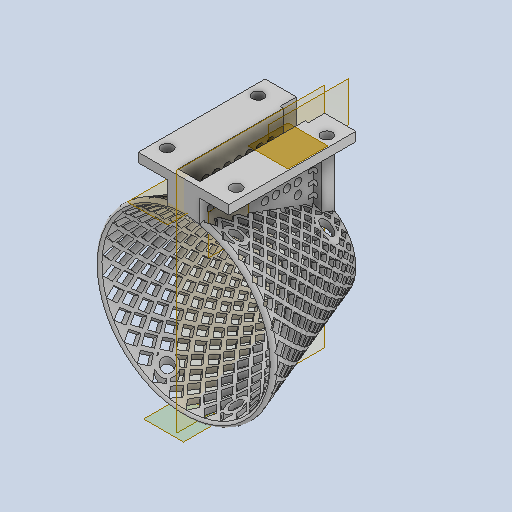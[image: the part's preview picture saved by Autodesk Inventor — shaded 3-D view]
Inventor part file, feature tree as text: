
AUTODESK INVENTOR PART (.ipt)
format: ipt  version: 2024 (Build 280153000, 153)  size: 3,942,912 bytes
history: native  units: mm
features: extrude x11, plane x9, other x7, sketch x4, reference x3, projected_geometry x2, pattern_circular x1, fillet x1
ambient origin geometry x8: Origin, YZ Plane, XZ Plane, XY Plane, X Axis, Y Axis, Z Axis, Center Point
bodies: Solid1 (feature_tree)
feature tree (38):
  plane  "Work Plane1"
  other  "hoop revolution"
  extrude  "net holes"  Depth=25.0mm
  pattern_circular  "Circular Pattern3"  Count=3  [1 undecoded]
  plane  "Work Plane15"
  extrude  "hoop slot"  TaperAngle=90.0deg  [1 undecoded]
  plane  "Work Plane10"
  extrude  "slot walls"  Depth=3.0mm
  plane  "Work Plane12"
  extrude  "arm holes"  Depth=10.0mm
  plane  "Work Plane11"
  sketch  "Sketch19"  dims[d364=50.0mm d365=3.0mm]
  plane  "Work Plane13"
  extrude  "mount holes extrusion"  Depth=10.0mm
  plane  "Work Plane16"
  extrude  "mounting holes and access holes"  Depth=10.0mm
  plane  "Work Plane18"
  extrude  "Extrusion13"  Depth=10.0mm
  plane  "Work Plane21"
  extrude  "back net reinforcement"  Depth=10.0mm
  fillet  "Fillet1"  Radius=1.0mm
  other  "middle plane for part"
  extrude  "Extrusion16"  Depth=10.0mm
  extrude  "Extrusion17"  Depth=10.0mm
  extrude  "Extrusion18"  Depth=10.0mm
  reference  "Reference1"
  reference  "Reference2"
  reference  "Reference3"
  other  "best net sketch"
  projected_geometry  "Projected Loop3"
  sketch  "Sketch16"  dims[d1=70.0mm d2=25.0mm d3=30.0mm]
  sketch  "Sketch17"  dims[d5=3.0mm d6=90.0deg]
  projected_geometry  "Projected Loop4"
  sketch  "Sketch22"  dims[d380=1.0mm d382=1.0mm d383=1.0mm d384=1.0mm d385=1.0mm d386=1.0mm d387=1.0mm d388=1.0mm d389=1.0mm d390=1.0mm d391=1.0mm d392=1.0mm d393=1.0mm d394=1.0mm d395=1.0mm d396=1.0mm d397=0.0mm d398=0.0mm d399=3.572329mm d400=0.0mm d401=300.0mm d402=360.0deg d404=10.0mm d406=20.0mm d407=0.0mm d408=1.0mm d409=18.099mm d410=0.0mm d411=1.0mm d412=3.0mm d413=50.0mm d414=0.0mm d417=10.0mm d418=0.0mm d419=0.0mm d420=55.0mm d423=3.0mm d424=4.5mm d426=10.0mm d431=5.0mm d432=0.0mm d433=6.0mm d434=6.0mm d439=10.0mm d440=10.0mm d441=6.2mm d442=20.0mm d444=50.0mm d445=20.0mm d447=38.0mm d450=0.0mm d451=0.0mm d452=10.0mm d453=10.0mm d454=10.0mm d455=0.0mm d456=10.0mm d457=10.0mm d458=10.0mm d459=10.0mm d460=10.0mm d461=10.0mm d462=10.0mm d463=0.0mm d464=12.277724mm d465=12.278391mm d466=4.1mm d467=50.0mm d469=5.0mm d470=10.0mm d472=10.0mm d478=2.0mm d479=70.0mm d481=6.0mm d482=30.0mm d484=6.0mm d487=40.0mm d489=6.0mm d490=10.0mm d492=10.0mm d494=60.0mm d496=6.0mm d497=10.0mm d499=10.0mm d508=10.0mm d509=0.0mm d510=60.0mm d512=6.0mm d513=10.0mm d515=0.0mm d517=10.0mm d518=0.0mm d519=2.8mm d520=2.8mm d523=6.5mm d524=8.0mm d525=6.5mm d526=8.0mm d532=40.0mm d533=0.0mm d538=1.0mm d539=1.0mm d540=15.6mm d541=8.933823mm]
  other  "net reinforcement"
  parser-record x1  (decoder bookkeeping rows leaked as tree rows — omitted from the tree; the rows remain in map.json)
  other  "BASKETBALL HOOP.iam"
  other  "BALL BEARING ARM:1"
note: 2 required parameter values undecoded (feature->parameter linkage not recoverable at this tier; creation-order binding heuristic only, values carry confidence <= 0.55)
note: 1 file-system path scrubbed to <path> (originals preserved in map.json)
